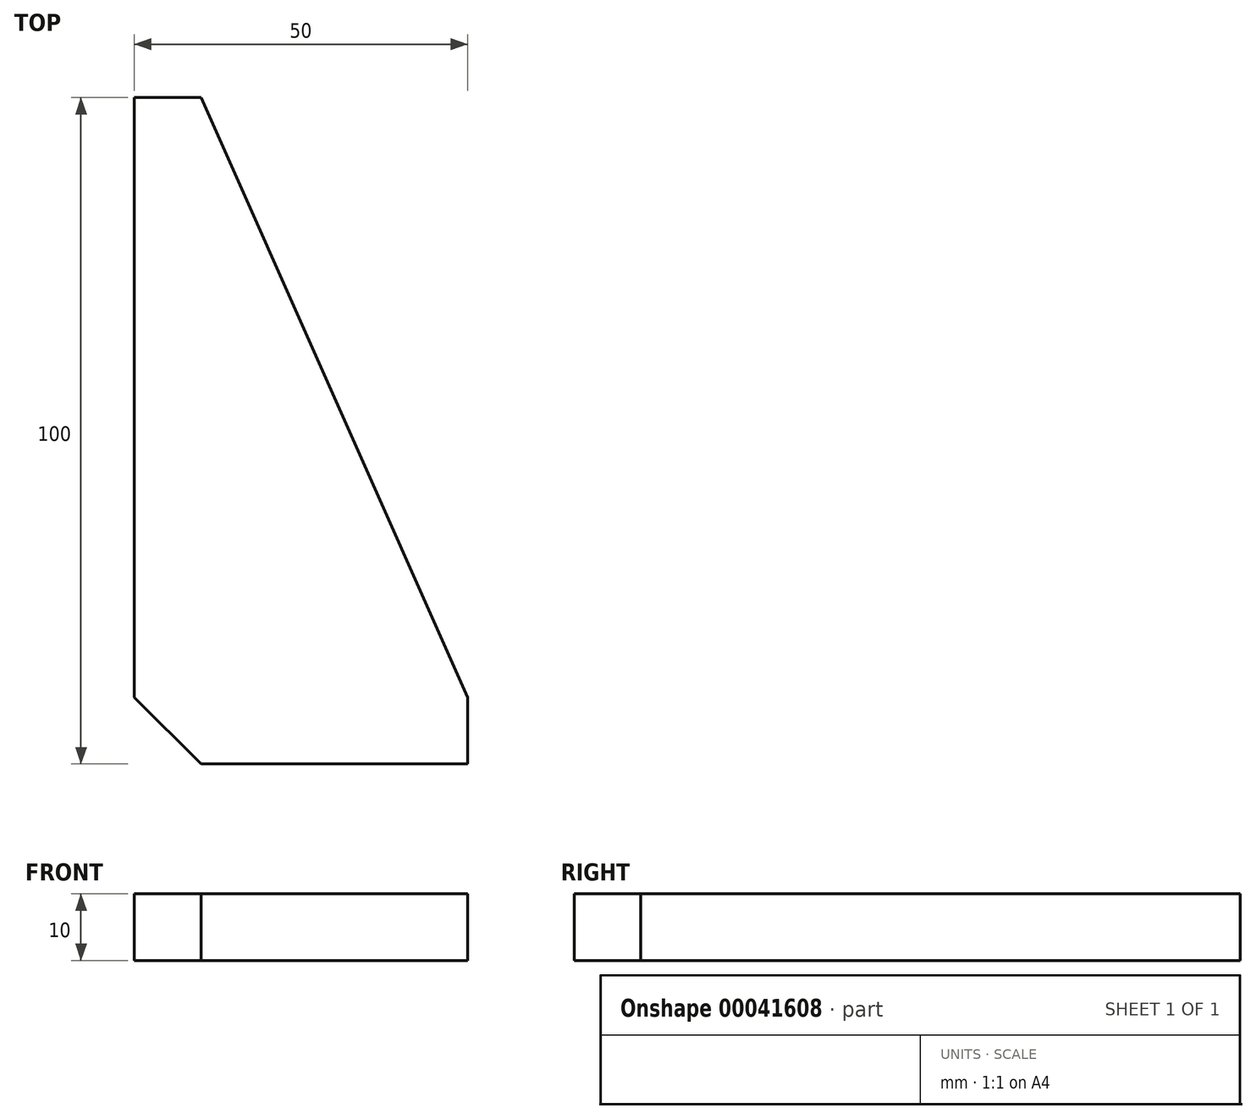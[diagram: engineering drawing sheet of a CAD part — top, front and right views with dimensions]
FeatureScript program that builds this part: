
annotation { "Feature Type Name" : "Feature", "Feature Type Description" : "" }
export const myFeature = defineFeature(function(context is Context, id is Id, definition is map)
    precondition{}
    {
        {
            var Q0;
            Q0=qCreatedBy(makeId("Top.planeOp"),FACE);
            var sketch = newSketch(context, id + "F0", { "sketchPlane" : qUnion([Q0])});
            skLineSegment(sketch, "E0.rect.bottom", {"start": v(-25, 50) * mm, "end": v(25, 50) * mm});
            skLineSegment(sketch, "E0.rect.top", {"start": v(-25, -50) * mm, "end": v(25, -50) * mm});
            skLineSegment(sketch, "E0.rect.left", {"start": v(-25, 50) * mm, "end": v(-25, -50) * mm});
            skLineSegment(sketch, "E0.rect.right", {"start": v(25, 50) * mm, "end": v(25, -50) * mm});
            skPoint(sketch, "E0.rect.middle", {"position": v(0, 0) * mm});
            skSolve(sketch);
        }
        {
            var Q0;
            Q0=makeQuery(id+"F0.imprint","IMPRINT",FACE,{"disambiguationData":[TD([[makeQuery(id+"F0.imprint","IMPRINT",EDGE,{"derivedFrom":sQuery(id+"F0.wireOp",EDGE,"E0.rect.bottom")}),-1.0]])]});
            extrude(context, id + "F1", {"entities" : qUnion([Q0]), "depth" : 10 * mm});
        }
        {
            var Q0;
            Q0=makeQuery(id+"F1.opExtrude","SWEPT_EDGE",EDGE,{"disambiguationData":[OSD([sQuery(id+"F0.wireOp",EDGE,"E0.rect.top"),sQuery(id+"F0.wireOp",EDGE,"E0.rect.left")])]});
            chamfer(context, id + "F2", {"entities" : qUnion([Q0]), "width" : 10 * mm, "tangentPropagation" : true});
        }
        {
            var Q0;
            Q0=makeQuery(id+"F1.opExtrude","CAP_FACE",FACE,{"disambiguationData":[OSD([sQuery(id+"F0.wireOp",EDGE,"E0.rect.bottom"),sQuery(id+"F0.wireOp",EDGE,"E0.rect.top"),sQuery(id+"F0.wireOp",EDGE,"E0.rect.left"),sQuery(id+"F0.wireOp",EDGE,"E0.rect.right")])],"isStart":false});
            var sketch = newSketch(context, id + "F3", { "sketchPlane" : qUnion([Q0])});
            skLineSegment(sketch, "E1", {"start": v(-15, -50) * mm, "end": v(-15, 50) * mm, "construction": true});
            skLineSegment(sketch, "E2", {"start": v(-25, -40) * mm, "end": v(25, -40) * mm, "construction": true});
            skLineSegment(sketch, "E3", {"start": v(-15, 50) * mm, "end": v(25, -40) * mm});
            skLineSegment(sketch, "E4", {"start": v(-15, 50) * mm, "end": v(25, 50) * mm});
            skLineSegment(sketch, "E5", {"start": v(25, 50) * mm, "end": v(25, -40) * mm});
            skSolve(sketch);
        }
        {
            var Q0;
            Q0=qSketchRegion(id+"F3",true);
            extrude(context, id + "F4", {"entities" : qUnion([Q0]), "operationType" : NewBodyOperationType.REMOVE, "endBound" : BoundingType.THROUGH_ALL, "oppositeDirection" : true, "depth" : 25 * mm});
        }
    });
